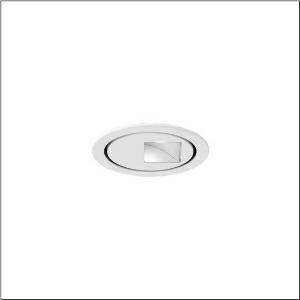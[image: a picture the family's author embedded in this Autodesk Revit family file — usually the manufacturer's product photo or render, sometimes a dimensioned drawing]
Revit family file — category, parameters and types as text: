
# Revit family: lunis_11_micro_round_51dj11b71wn21
name_source: partatom
category: Lighting Fixtures
units: mm (PartAtom-declared; Revit-internal decimal feet)

## family parameters
Cut with Voids When Loaded = No
Host = Face
Light Source = No
Part Type = Normal
Room Calculation Point = No
Round Connector Dimension = Use Diameter
Shared = No

## types (1)
- Lunis 11 micro round (1 x LED 4000K / CRI = 90 (unbekannt), 1210 lm, 4000K)
    Apparent Load = 20 VA
    CIE Flux Codes = 42 75 96 100 100
    Color Rendering = 90
    Color Temperature = 4000K
    Default Elevation = 1800 mm
    Description = Lunis 11 micro round, downlight, light control with wallwasher, of highly reflective aluminium, highly specular, light emission: direct distribution, LED rated luminous flux: 1.210lm, light colour: 940, with terminal, 3-pole, mains connection: 220..230V, AC, 50/60Hz, LED module, of aluminium, highly specular, white, diameter: 114mm, clamping range: 1..40mm, recessing ring, of plastic, traffic white (RAL 9016), protection rating (complete): IP20, insulation class (complete): insulation class II (safety insulation), certification: CE, permissible ambient temperature for indoor applications: 0..+35°C, packaging unit: 1 piece
    Height = 0 mm  [stored 0 ft]
    Lamp = 1 x LED 4000K / CRI >= 90 (unbekannt)
    Lamp Light Flux = 1210 lm
    Lamp count = 1
    Length = 114 mm
    Luminous efficacy = 61 lm/W
    Manufacturer = Siteco
    ModVariant = No
    Model = 51DJ11B71WN21
    Mounting Place = Ceiling
    Mounting Type = Recessed
    Number of Poles = 1
    OnlyDefault = Yes
    Power Factor = 1
    Product Name = Lunis 11 micro round
    Product group = downlight
    ProductGroupID = 400
    Protection Class = Protection class II
    Protection Degree = IP 20
    RLX_Detail_Level = 1
    RLX_Emergency_Light_Flux = 0 lm
    RLX_Emergency_Type = 0
    RLX_Emergency_Type_DB = No
    RlxData = <blob elided: 40829 chars, md5=9cbdabbf>
    Socket = socket
    Standby Power = 0 W
    System Light Flux = 1210 lm
    System Power = 20 W
    Type Comments = Product without accessories
    Type Image = l_1004773.jpg
    URL = http://relux.com
    VarID = ---
    Voltage = 0 V
    Weight = 0.00 kg
    Width = 114 mm

note: [stored X ft] marks values corroborated as IEEE doubles in the binary element streams (Revit-internal decimal feet)

## geometry (parser evidence)
native form markers: Blend x4, Sweep x9
no freeform markers — native parametric forms only
